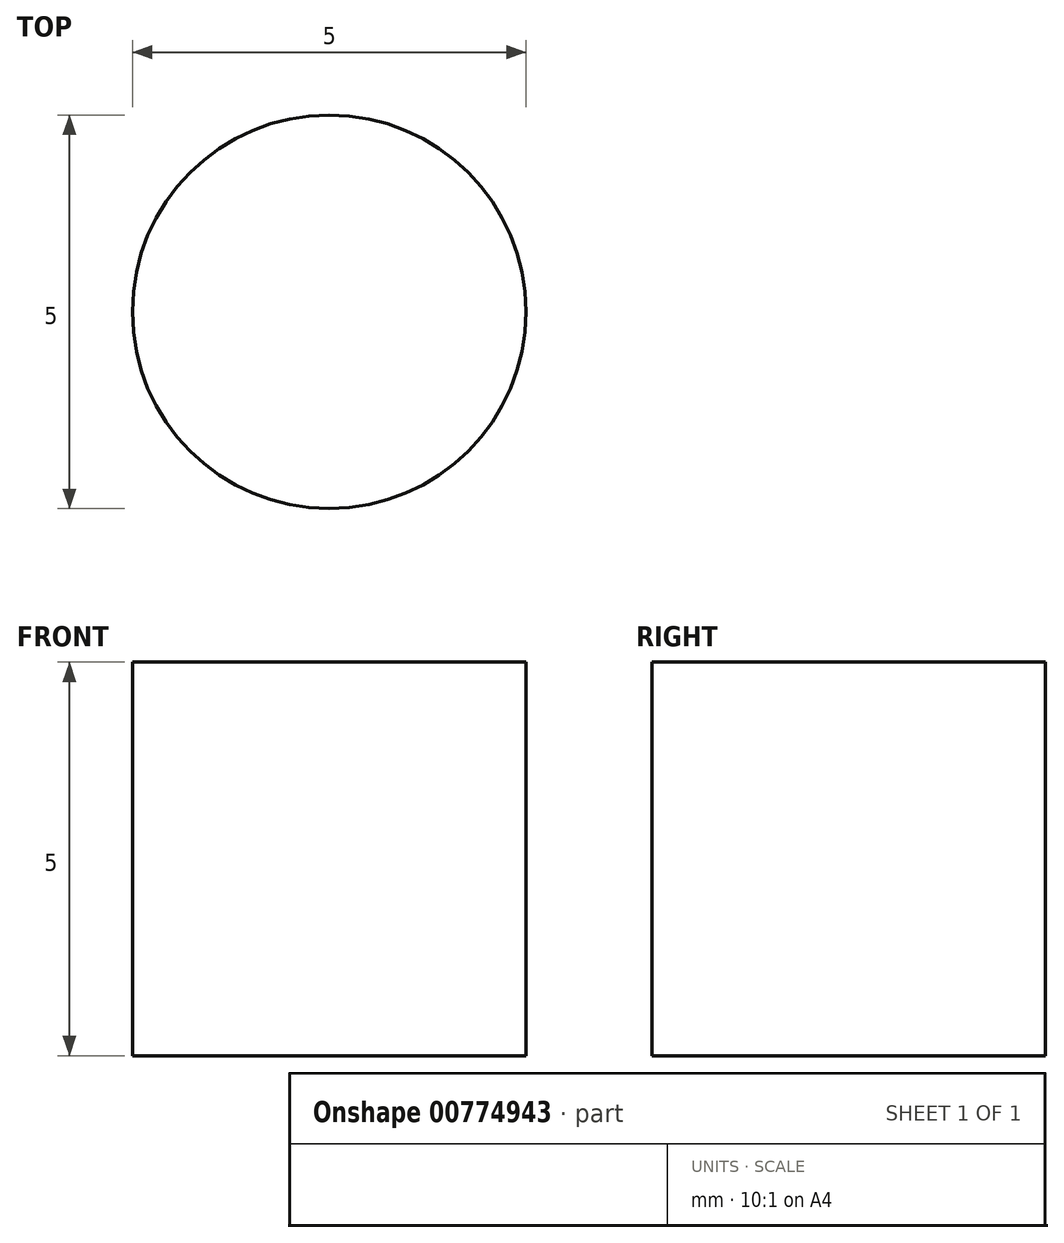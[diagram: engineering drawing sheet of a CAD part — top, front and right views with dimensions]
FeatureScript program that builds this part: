
annotation { "Feature Type Name" : "Feature", "Feature Type Description" : "" }
export const myFeature = defineFeature(function(context is Context, id is Id, definition is map)
    precondition{}
    {
        {
            var Q0;
            Q0=qCreatedBy(makeId("Top.planeOp"),FACE);
            var sketch = newSketch(context, id + "F0", { "sketchPlane" : qUnion([Q0])});
            skCircle(sketch, "E0", {"center": v(0, 0) * mm, "radius": 2.5 * mm});
            skSolve(sketch);
        }
        {
            var Q0;
            Q0 = qSketchRegion(id + "F0", true);
            extrude(context, id + "F1", {"entities" : qUnion([Q0]), "depth" : 5 * mm, "offsetDistance" : 25 * mm});
        }
    });
